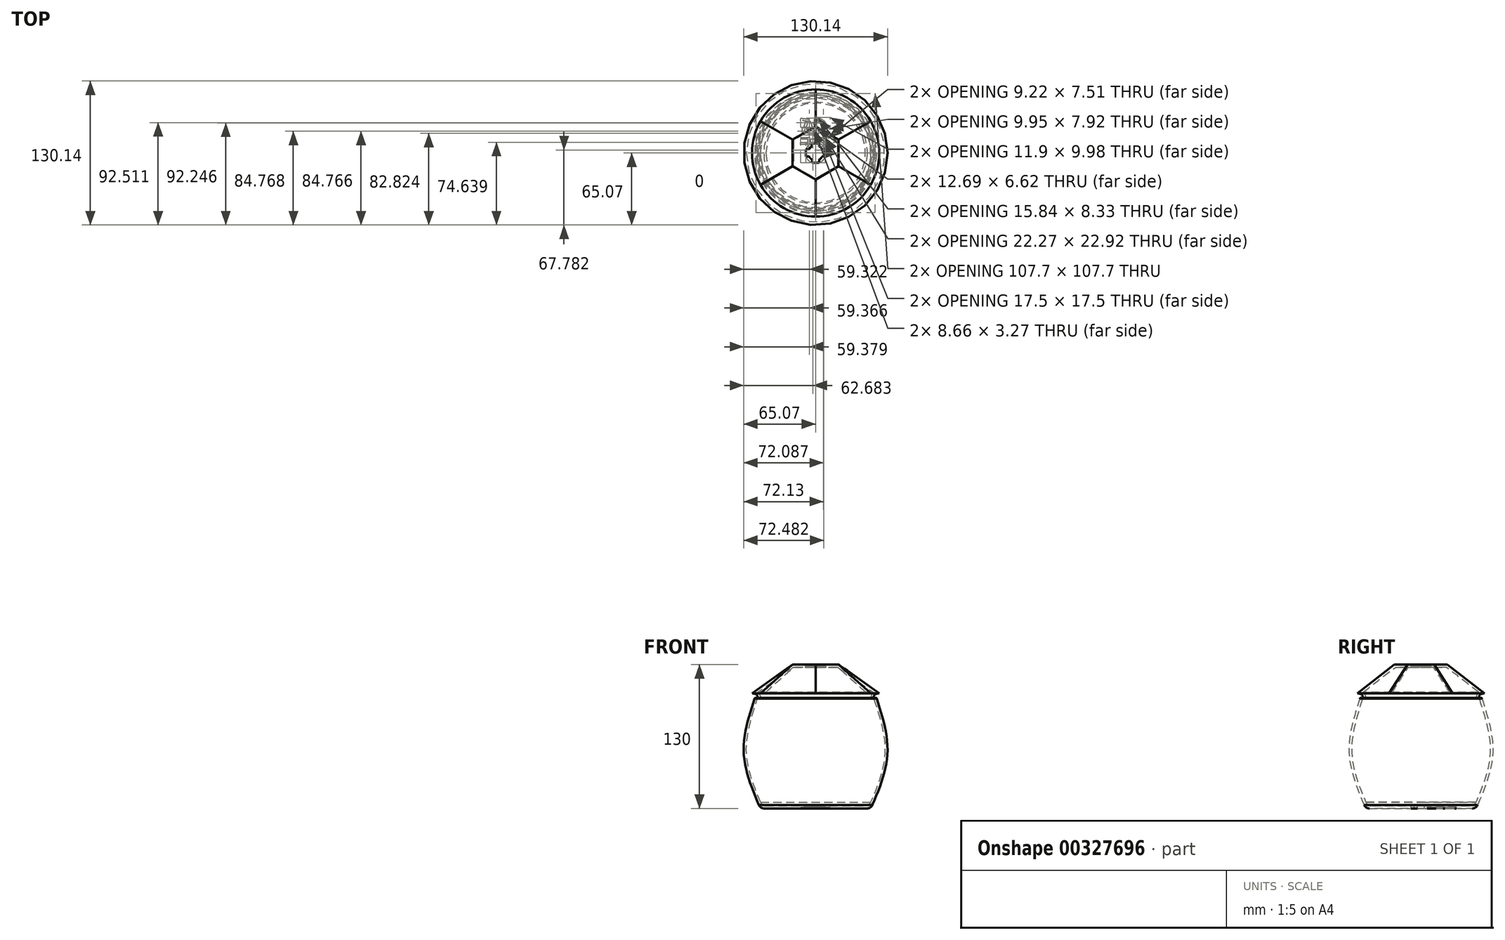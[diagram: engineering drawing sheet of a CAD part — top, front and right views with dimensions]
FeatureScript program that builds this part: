
annotation { "Feature Type Name" : "Feature", "Feature Type Description" : "" }
export const myFeature = defineFeature(function(context is Context, id is Id, definition is map)
    precondition{}
    {
        {
            var Q0;
            Q0=qCreatedBy(makeId("Top.planeOp"),FACE);
            var sketch = newSketch(context, id + "F0", { "sketchPlane" : qUnion([Q0])});
            skCircle(sketch, "E0", {"center": v(0, 0) * mm, "radius": 50 * mm});
            skSolve(sketch);
        }
        {
            var Q0;
            Q0=qCreatedBy(makeId("Top.planeOp"),FACE);
            cPlane(context, id + "F1", {"entities" : qUnion([Q0]), "cplaneType" : CPlaneType.OFFSET, "offset" : 50 * mm, "width" : 150 * mm, "height" : 150 * mm});
        }
        {
            var Q0;
            Q0=qCreatedBy(id+"F1.planeOp",FACE);
            cPlane(context, id + "F2", {"entities" : qUnion([Q0]), "cplaneType" : CPlaneType.OFFSET, "offset" : 50 * mm, "width" : 150 * mm, "height" : 150 * mm});
        }
        {
            var Q0;
            Q0=qCreatedBy(id+"F1.planeOp",FACE);
            var sketch = newSketch(context, id + "F3", { "sketchPlane" : qUnion([Q0])});
            skCircle(sketch, "E1", {"center": v(0, 0) * mm, "radius": 65 * mm});
            skSolve(sketch);
        }
        {
            var Q0;
            Q0=qCreatedBy(id+"F2.planeOp",FACE);
            var sketch = newSketch(context, id + "F4", { "sketchPlane" : qUnion([Q0])});
            skCircle(sketch, "E2", {"center": v(0, 0) * mm, "radius": 55 * mm});
            skSolve(sketch);
        }
        {
            var Q0;
            Q0=makeQuery(id+"F0.imprint","IMPRINT",FACE,{"disambiguationData":[TD([[makeQuery(id+"F0.imprint","IMPRINT",EDGE,{"derivedFrom":sQuery(id+"F0.wireOp",EDGE,"E0")}),1.0]])]});
            var Q1;
            Q1=makeQuery(id+"F3.imprint","IMPRINT",FACE,{"disambiguationData":[TD([[makeQuery(id+"F3.imprint","IMPRINT",EDGE,{"derivedFrom":sQuery(id+"F3.wireOp",EDGE,"E1")}),1.0]])]});
            var Q2;
            Q2=makeQuery(id+"F4.imprint","IMPRINT",FACE,{"disambiguationData":[TD([[makeQuery(id+"F4.imprint","IMPRINT",EDGE,{"derivedFrom":sQuery(id+"F4.wireOp",EDGE,"E2")}),1.0]])]});
            loft(context, id + "F5", {"sheetProfilesArray" : [{ "sheetProfileEntities" : qUnion([Q0]) }, { "sheetProfileEntities" : qUnion([Q1]) }, { "sheetProfileEntities" : qUnion([Q2]) }]});
        }
        {
            var Q0;
            Q0=makeQuery(id+"F5.opLoft","CAP_FACE",FACE,{"disambiguationData":[OSD([makeQuery(id+"F4.imprint","IMPRINT",FACE,{"disambiguationData":[TD([[makeQuery(id+"F4.imprint","IMPRINT",EDGE,{"derivedFrom":sQuery(id+"F4.wireOp",EDGE,"E2")}),1.0]])]})])],"isStart":true});
            shell(context, id + "F6", {"entities" : qUnion([Q0]), "thickness" : 2.4 * mm});
        }
        {
            var Q0;
            Q0=makeQuery(id+"F6.opShell","OFFSET_EDGE",EDGE,{"disambiguationData":[OSD([sQuery(id+"F0.wireOp",EDGE,"E0")])]});
            var Q1;
            Q1=makeQuery(id+"F5.opLoft","MID_CAP_EDGE",EDGE,{"disambiguationData":[OSD([sQuery(id+"F0.wireOp",EDGE,"E0")])],"capPos":0.0});
            fillet(context, id + "F7", {"entities" : qUnion([Q0, Q1]), "radius" : 5 * mm, "tangentPropagation" : true, "allowEdgeOverflow" : false});
        }
        {
            var Q0;
            Q0=makeQuery(id+"F5.opLoft","MID_CAP_EDGE",EDGE,{"disambiguationData":[OSD([sQuery(id+"F0.wireOp",EDGE,"E0"),sQuery(id+"F4.wireOp",EDGE,"E2")])],"capPos":2.0});
            var Q1;
            Q1=makeQuery(id+"F6.opShell","OFFSET_EDGE",EDGE,{"disambiguationData":[OSD([sQuery(id+"F0.wireOp",EDGE,"E0"),sQuery(id+"F4.wireOp",EDGE,"E2")])]});
            fillet(context, id + "F8", {"entities" : qUnion([Q0, Q1]), "radius" : 1 * mm, "tangentPropagation" : true, "allowEdgeOverflow" : false});
        }
        {
            var Q0;
            Q0=qCreatedBy(id+"F2.planeOp",FACE);
            var sketch = newSketch(context, id + "F9", { "sketchPlane" : qUnion([Q0])});
            skCircle(sketch, "E3", {"center": v(0, 0) * mm, "radius": 52.5 * mm});
            skSolve(sketch);
        }
        {
            var Q0;
            Q0=qCreatedBy(id+"F2.planeOp",FACE);
            cPlane(context, id + "F10", {"entities" : qUnion([Q0]), "cplaneType" : CPlaneType.OFFSET, "offset" : 30 * mm, "width" : 150 * mm, "height" : 150 * mm});
        }
        {
            var Q0;
            Q0=qCreatedBy(id+"F10.planeOp",FACE);
            var sketch = newSketch(context, id + "F11", { "sketchPlane" : qUnion([Q0])});
            skCircle(sketch, "E4.cCircle", {"center": v(0, 0) * mm, "radius": 20.78 * mm, "construction": true});
            skLineSegment(sketch, "E4.0", {"start": v(0, 24) * mm, "end": v(20.79, 12) * mm});
            skLineSegment(sketch, "E4.1", {"start": v(20.79, 12) * mm, "end": v(20.78, -12) * mm});
            skLineSegment(sketch, "E4.2", {"start": v(20.78, -12) * mm, "end": v(0, -24) * mm});
            skLineSegment(sketch, "E4.3", {"start": v(0, -24) * mm, "end": v(-20.79, -12) * mm});
            skLineSegment(sketch, "E4.4", {"start": v(-20.79, -12) * mm, "end": v(-20.78, 12) * mm});
            skLineSegment(sketch, "E4.5", {"start": v(-20.78, 12) * mm, "end": v(0, 24) * mm});
            skPoint(sketch, "E4.0.midPoint", {"position": v(10.4, 18) * mm});
            skSolve(sketch);
        }
        {
            var Q0;
            Q0=qCreatedBy(id+"F2.planeOp",FACE);
            cPlane(context, id + "F12", {"entities" : qUnion([Q0]), "cplaneType" : CPlaneType.OFFSET, "offset" : 4 * mm, "width" : 150 * mm, "height" : 150 * mm});
        }
        {
            var Q0;
            Q0=qCreatedBy(id+"F12.planeOp",FACE);
            var sketch = newSketch(context, id + "F13", { "sketchPlane" : qUnion([Q0])});
            skCircle(sketch, "E5", {"center": v(0, 0) * mm, "radius": 57.5 * mm});
            skSolve(sketch);
        }
        {
            var Q0;
            Q0=makeQuery(id+"F9.imprint","IMPRINT",FACE,{"disambiguationData":[TD([[makeQuery(id+"F9.imprint","IMPRINT",EDGE,{"derivedFrom":sQuery(id+"F9.wireOp",EDGE,"E3")}),1.0]])]});
            var Q1;
            Q1=makeQuery(id+"F13.imprint","IMPRINT",FACE,{"disambiguationData":[TD([[makeQuery(id+"F13.imprint","IMPRINT",EDGE,{"derivedFrom":sQuery(id+"F13.wireOp",EDGE,"E5")}),1.0]])]});
            loft(context, id + "F14", {"startCondition" : LoftEndDerivativeType.NORMAL_TO_PROFILE, "startMagnitude" : 2.5, "sheetProfilesArray" : [{ "sheetProfileEntities" : qUnion([Q0]) }, { "sheetProfileEntities" : qUnion([Q1]) }]});
        }
        {
            var Q1;
            Q1=makeQuery(id+"F14.opLoft","CAP_FACE",FACE,{"disambiguationData":[OSD([makeQuery(id+"F13.imprint","IMPRINT",FACE,{"disambiguationData":[TD([[makeQuery(id+"F13.imprint","IMPRINT",EDGE,{"derivedFrom":sQuery(id+"F13.wireOp",EDGE,"E5")}),1.0]])]})])],"isStart":true});
            var Q2;
            Q2=makeQuery(id+"F11.imprint","IMPRINT",FACE,{"disambiguationData":[TD([[makeQuery(id+"F11.imprint","IMPRINT",EDGE,{"derivedFrom":sQuery(id+"F11.wireOp",EDGE,"E4.0")}),-1.0]])]});
            loft(context, id + "F15", {"operationType" : NewBodyOperationType.ADD, "sheetProfilesArray" : [{ "sheetProfileEntities" : qUnion([Q1]) }, { "sheetProfileEntities" : qUnion([Q2]) }]});
        }
        {
            var Q0;
            Q0=makeQuery(id+"F14.opLoft","CAP_FACE",FACE,{"disambiguationData":[OSD([makeQuery(id+"F9.imprint","IMPRINT",FACE,{"disambiguationData":[TD([[makeQuery(id+"F9.imprint","IMPRINT",EDGE,{"derivedFrom":sQuery(id+"F9.wireOp",EDGE,"E3")}),1.0]])]})])],"isStart":true});
            shell(context, id + "F16", {"entities" : qUnion([Q0]), "thickness" : 2.4 * mm});
        }
        {
            var Q0;
            Q0=makeQuery(id+"F15.opLoft","CAP_FACE",FACE,{"disambiguationData":[OSD([makeQuery(id+"F11.imprint","IMPRINT",FACE,{"disambiguationData":[TD([[makeQuery(id+"F11.imprint","IMPRINT",EDGE,{"derivedFrom":sQuery(id+"F11.wireOp",EDGE,"E4.0")}),-1.0]])]})])],"isStart":true});
            var sketch = newSketch(context, id + "F17", { "sketchPlane" : qUnion([Q0])});
            skCircle(sketch, "E6", {"center": v(0, 0) * mm, "radius": 6.75 * mm});
            skLineSegment(sketch, "E7", {"start": v(8.75, 3.25) * mm, "end": v(8.75, -3.25) * mm});
            skPoint(sketch, "E8", {"position": v(8.75, 0) * mm});
            skPoint(sketch, "E9", {"position": v(6.75, 0) * mm});
            skPoint(sketch, "E10", {"position": v(-6.75, 0) * mm});
            skPoint(sketch, "E11", {"position": v(0, -6.75) * mm});
            skPoint(sketch, "E12", {"position": v(0, 6.75) * mm});
            skLineSegment(sketch, "E13", {"start": v(8.75, 3.25) * mm, "end": v(5.92, 3.25) * mm});
            skLineSegment(sketch, "E14", {"start": v(8.75, -3.25) * mm, "end": v(5.92, -3.25) * mm});
            skPoint(sketch, "E15.1.0", {"position": v(0, 8.75) * mm});
            skLineSegment(sketch, "E15.1.2", {"start": v(-3.25, 8.75) * mm, "end": v(3.25, 8.75) * mm});
            skLineSegment(sketch, "E15.1.3", {"start": v(-3.25, 8.75) * mm, "end": v(-3.25, 5.92) * mm});
            skLineSegment(sketch, "E15.1.4", {"start": v(3.25, 8.75) * mm, "end": v(3.25, 5.92) * mm});
            skPoint(sketch, "E15.2.0", {"position": v(-8.75, 0) * mm});
            skLineSegment(sketch, "E15.2.2", {"start": v(-8.75, -3.25) * mm, "end": v(-8.75, 3.25) * mm});
            skLineSegment(sketch, "E15.2.3", {"start": v(-8.75, -3.25) * mm, "end": v(-5.92, -3.25) * mm});
            skLineSegment(sketch, "E15.2.4", {"start": v(-8.75, 3.25) * mm, "end": v(-5.92, 3.25) * mm});
            skPoint(sketch, "E15.3.0", {"position": v(0, -8.75) * mm});
            skLineSegment(sketch, "E15.3.2", {"start": v(3.25, -8.75) * mm, "end": v(-3.25, -8.75) * mm});
            skLineSegment(sketch, "E15.3.3", {"start": v(3.25, -8.75) * mm, "end": v(3.25, -5.92) * mm});
            skLineSegment(sketch, "E15.3.4", {"start": v(-3.25, -8.75) * mm, "end": v(-3.25, -5.92) * mm});
            skSolve(sketch);
        }
        {
            var Q0;
            {var subQ0=sQuery(id+"F17.wireOp",EDGE,"E6");var subQ5=makeQuery(id+"F17.imprint","INTERSECT",VERTEX,{"derivedFrom":[subQ0,sQuery(id+"F17.wireOp",EDGE,"E13")]});Q0=makeQuery(id+"F17.imprint","IMPRINT",FACE,{"disambiguationData":[TD([[makeQuery(id+"F17.imprint","IMPRINT",EDGE,{"disambiguationData":[TD([[subQ5,-1.0]])],"derivedFrom":subQ0}),1.0]])]});}
            var Q1;
            Q1=makeQuery(id+"F17.imprint","IMPRINT",FACE,{"disambiguationData":[TD([[makeQuery(id+"F17.imprint","IMPRINT",EDGE,{"derivedFrom":sQuery(id+"F17.wireOp",EDGE,"E15.1.2")}),-1.0]])]});
            var Q2;
            Q2=makeQuery(id+"F17.imprint","IMPRINT",FACE,{"disambiguationData":[TD([[makeQuery(id+"F17.imprint","IMPRINT",EDGE,{"derivedFrom":sQuery(id+"F17.wireOp",EDGE,"E7")}),-1.0]])]});
            var Q3;
            Q3=makeQuery(id+"F17.imprint","IMPRINT",FACE,{"disambiguationData":[TD([[makeQuery(id+"F17.imprint","IMPRINT",EDGE,{"derivedFrom":sQuery(id+"F17.wireOp",EDGE,"E15.3.2")}),-1.0]])]});
            var Q4;
            Q4=makeQuery(id+"F17.imprint","IMPRINT",FACE,{"disambiguationData":[TD([[makeQuery(id+"F17.imprint","IMPRINT",EDGE,{"derivedFrom":sQuery(id+"F17.wireOp",EDGE,"E15.2.2")}),-1.0]])]});
            extrude(context, id + "F18", {"entities" : qUnion([Q0, Q1, Q2, Q3, Q4]), "operationType" : NewBodyOperationType.REMOVE, "endBound" : BoundingType.THROUGH_ALL, "oppositeDirection" : true, "depth" : 25 * mm});
        }
        {
            var Q0;
            Q0=makeQuery(id+"F16.opShell","OFFSET_FACE",FACE,{"disambiguationData":[OSD([makeQuery(id+"F11.imprint","IMPRINT",FACE,{"disambiguationData":[TD([[makeQuery(id+"F11.imprint","IMPRINT",EDGE,{"derivedFrom":sQuery(id+"F11.wireOp",EDGE,"E4.0")}),-1.0]])]})])]});
            var sketch = newSketch(context, id + "F19", { "sketchPlane" : qUnion([Q0])});
            skCircle(sketch, "E16", {"center": v(0, 0) * mm, "radius": 9.33 * mm});
            skSolve(sketch);
        }
        {
            var Q0;
            {var subQ1=sQuery(id+"F17.wireOp",EDGE,"E15.2.3");var subQ2=makeQuery(id+"F16.opShell","OFFSET_FACE",FACE,{"disambiguationData":[OSD([makeQuery(id+"F11.imprint","IMPRINT",FACE,{"disambiguationData":[TD([[makeQuery(id+"F11.imprint","IMPRINT",EDGE,{"derivedFrom":sQuery(id+"F11.wireOp",EDGE,"E4.0")}),-1.0]])]})])]});var subQ3=makeQuery(id+"F18.boolean.opBoolean","INTERSECT",EDGE,{"derivedFrom":[subQ2,makeQuery(id+"F18.opExtrude","SWEPT_FACE",FACE,{"disambiguationData":[OSD([subQ1])]})]});Q0=makeQuery(id+"F19.imprint","IMPRINT",FACE,{"disambiguationData":[TD([[makeQuery(id+"F19.imprint","IMPRINT",EDGE,{"derivedFrom":subQ3}),1.0]])]});}
            var Q1;
            {var subQ1=sQuery(id+"F17.wireOp",EDGE,"E15.1.3");var subQ2=makeQuery(id+"F16.opShell","OFFSET_FACE",FACE,{"disambiguationData":[OSD([makeQuery(id+"F11.imprint","IMPRINT",FACE,{"disambiguationData":[TD([[makeQuery(id+"F11.imprint","IMPRINT",EDGE,{"derivedFrom":sQuery(id+"F11.wireOp",EDGE,"E4.0")}),-1.0]])]})])]});var subQ3=makeQuery(id+"F18.boolean.opBoolean","INTERSECT",EDGE,{"derivedFrom":[subQ2,makeQuery(id+"F18.opExtrude","SWEPT_FACE",FACE,{"disambiguationData":[OSD([subQ1])]})]});Q1=makeQuery(id+"F19.imprint","IMPRINT",FACE,{"disambiguationData":[TD([[makeQuery(id+"F19.imprint","IMPRINT",EDGE,{"derivedFrom":subQ3}),1.0]])]});}
            var Q2;
            {var subQ1=makeQuery(id+"F16.opShell","OFFSET_FACE",FACE,{"disambiguationData":[OSD([makeQuery(id+"F11.imprint","IMPRINT",FACE,{"disambiguationData":[TD([[makeQuery(id+"F11.imprint","IMPRINT",EDGE,{"derivedFrom":sQuery(id+"F11.wireOp",EDGE,"E4.0")}),-1.0]])]})])]});var subQ2=makeQuery(id+"F18.boolean.opBoolean","INTERSECT",EDGE,{"derivedFrom":[subQ1,makeQuery(id+"F18.opExtrude","SWEPT_FACE",FACE,{"disambiguationData":[OSD([sQuery(id+"F17.wireOp",EDGE,"E15.2.2")])]})]});Q2=makeQuery(id+"F19.imprint","IMPRINT",FACE,{"disambiguationData":[TD([[makeQuery(id+"F19.imprint","IMPRINT",EDGE,{"derivedFrom":subQ2}),-1.0]])]});}
            var Q3;
            {var subQ1=makeQuery(id+"F16.opShell","OFFSET_FACE",FACE,{"disambiguationData":[OSD([makeQuery(id+"F11.imprint","IMPRINT",FACE,{"disambiguationData":[TD([[makeQuery(id+"F11.imprint","IMPRINT",EDGE,{"derivedFrom":sQuery(id+"F11.wireOp",EDGE,"E4.0")}),-1.0]])]})])]});var subQ2=makeQuery(id+"F18.boolean.opBoolean","INTERSECT",EDGE,{"derivedFrom":[subQ1,makeQuery(id+"F18.opExtrude","SWEPT_FACE",FACE,{"disambiguationData":[OSD([sQuery(id+"F17.wireOp",EDGE,"E15.1.2")])]})]});Q3=makeQuery(id+"F19.imprint","IMPRINT",FACE,{"disambiguationData":[TD([[makeQuery(id+"F19.imprint","IMPRINT",EDGE,{"derivedFrom":subQ2}),-1.0]])]});}
            var Q4;
            {var subQ1=sQuery(id+"F17.wireOp",EDGE,"E13");var subQ2=makeQuery(id+"F16.opShell","OFFSET_FACE",FACE,{"disambiguationData":[OSD([makeQuery(id+"F11.imprint","IMPRINT",FACE,{"disambiguationData":[TD([[makeQuery(id+"F11.imprint","IMPRINT",EDGE,{"derivedFrom":sQuery(id+"F11.wireOp",EDGE,"E4.0")}),-1.0]])]})])]});var subQ3=makeQuery(id+"F18.boolean.opBoolean","INTERSECT",EDGE,{"derivedFrom":[subQ2,makeQuery(id+"F18.opExtrude","SWEPT_FACE",FACE,{"disambiguationData":[OSD([subQ1])]})]});Q4=makeQuery(id+"F19.imprint","IMPRINT",FACE,{"disambiguationData":[TD([[makeQuery(id+"F19.imprint","IMPRINT",EDGE,{"derivedFrom":subQ3}),1.0]])]});}
            var Q5;
            {var subQ1=makeQuery(id+"F16.opShell","OFFSET_FACE",FACE,{"disambiguationData":[OSD([makeQuery(id+"F11.imprint","IMPRINT",FACE,{"disambiguationData":[TD([[makeQuery(id+"F11.imprint","IMPRINT",EDGE,{"derivedFrom":sQuery(id+"F11.wireOp",EDGE,"E4.0")}),-1.0]])]})])]});var subQ2=makeQuery(id+"F18.boolean.opBoolean","INTERSECT",EDGE,{"derivedFrom":[subQ1,makeQuery(id+"F18.opExtrude","SWEPT_FACE",FACE,{"disambiguationData":[OSD([sQuery(id+"F17.wireOp",EDGE,"E7")])]})]});Q5=makeQuery(id+"F19.imprint","IMPRINT",FACE,{"disambiguationData":[TD([[makeQuery(id+"F19.imprint","IMPRINT",EDGE,{"derivedFrom":subQ2}),-1.0]])]});}
            var Q6;
            {var subQ1=sQuery(id+"F17.wireOp",EDGE,"E14");var subQ2=makeQuery(id+"F16.opShell","OFFSET_FACE",FACE,{"disambiguationData":[OSD([makeQuery(id+"F11.imprint","IMPRINT",FACE,{"disambiguationData":[TD([[makeQuery(id+"F11.imprint","IMPRINT",EDGE,{"derivedFrom":sQuery(id+"F11.wireOp",EDGE,"E4.0")}),-1.0]])]})])]});var subQ3=makeQuery(id+"F18.boolean.opBoolean","INTERSECT",EDGE,{"derivedFrom":[subQ2,makeQuery(id+"F18.opExtrude","SWEPT_FACE",FACE,{"disambiguationData":[OSD([subQ1])]})]});Q6=makeQuery(id+"F19.imprint","IMPRINT",FACE,{"disambiguationData":[TD([[makeQuery(id+"F19.imprint","IMPRINT",EDGE,{"derivedFrom":subQ3}),-1.0]])]});}
            extrude(context, id + "F20", {"entities" : qUnion([Q0, Q1, Q2, Q3, Q4, Q5, Q6]), "operationType" : NewBodyOperationType.REMOVE, "oppositeDirection" : true, "depth" : 1 * mm});
        }
        {
            var Q0;
            Q0=makeQuery(id+"F5.opLoft","CAP_FACE",FACE,{"disambiguationData":[OSD([makeQuery(id+"F0.imprint","IMPRINT",FACE,{"disambiguationData":[TD([[makeQuery(id+"F0.imprint","IMPRINT",EDGE,{"derivedFrom":sQuery(id+"F0.wireOp",EDGE,"E0")}),1.0]])]})])],"isStart":true});
            var sketch = newSketch(context, id + "F21", { "sketchPlane" : qUnion([Q0])});
            skText(sketch, "E17", { "text": "彭", "fontName": "NotoSansCJKtc-Regular.otf"});
            const initialGuessF21  = {"E17": [-0.01523, -0.0299, 1, 0, 0.0212]};
            skSetInitialGuess(sketch, initialGuessF21);
            skSolve(sketch);
        }
        {
            var Q0;
            Q0=makeQuery(id+"F21.imprint","IMPRINT",FACE,{"disambiguationData":[TD([[makeQuery(id+"F21.imprint","IMPRINT",EDGE,{"derivedFrom":sQuery(id+"F21.wireOp",EDGE,"E17.sketch_text.stroke-44")}),1.0]])]});
            var Q1;
            Q1=makeQuery(id+"F21.imprint","IMPRINT",FACE,{"disambiguationData":[TD([[makeQuery(id+"F21.imprint","IMPRINT",EDGE,{"derivedFrom":sQuery(id+"F21.wireOp",EDGE,"E17.sketch_text.stroke-4")}),1.0]])]});
            var Q2;
            Q2=makeQuery(id+"F21.imprint","IMPRINT",FACE,{"disambiguationData":[TD([[makeQuery(id+"F21.imprint","IMPRINT",EDGE,{"derivedFrom":sQuery(id+"F21.wireOp",EDGE,"E17.sketch_text.stroke-0")}),1.0]])]});
            var Q3;
            Q3=makeQuery(id+"F21.imprint","IMPRINT",FACE,{"disambiguationData":[TD([[makeQuery(id+"F21.imprint","IMPRINT",EDGE,{"derivedFrom":sQuery(id+"F21.wireOp",EDGE,"E17.sketch_text.stroke-8")}),1.0]])]});
            var Q4;
            Q4=makeQuery(id+"F21.imprint","IMPRINT",FACE,{"disambiguationData":[TD([[makeQuery(id+"F21.imprint","IMPRINT",EDGE,{"derivedFrom":sQuery(id+"F21.wireOp",EDGE,"E17.sketch_text.stroke-24")}),1.0]])]});
            var Q5;
            Q5=makeQuery(id+"F21.imprint","IMPRINT",FACE,{"disambiguationData":[TD([[makeQuery(id+"F21.imprint","IMPRINT",EDGE,{"derivedFrom":sQuery(id+"F21.wireOp",EDGE,"E17.sketch_text.stroke-36")}),1.0]])]});
            var Q6;
            Q6=makeQuery(id+"F21.imprint","IMPRINT",FACE,{"disambiguationData":[TD([[makeQuery(id+"F21.imprint","IMPRINT",EDGE,{"derivedFrom":sQuery(id+"F21.wireOp",EDGE,"E17.sketch_text.stroke-32")}),1.0]])]});
            extrude(context, id + "F22", {"entities" : qUnion([Q0, Q1, Q2, Q3, Q4, Q5, Q6]), "operationType" : NewBodyOperationType.REMOVE, "oppositeDirection" : true, "depth" : 0.8 * mm});
        }
    });
